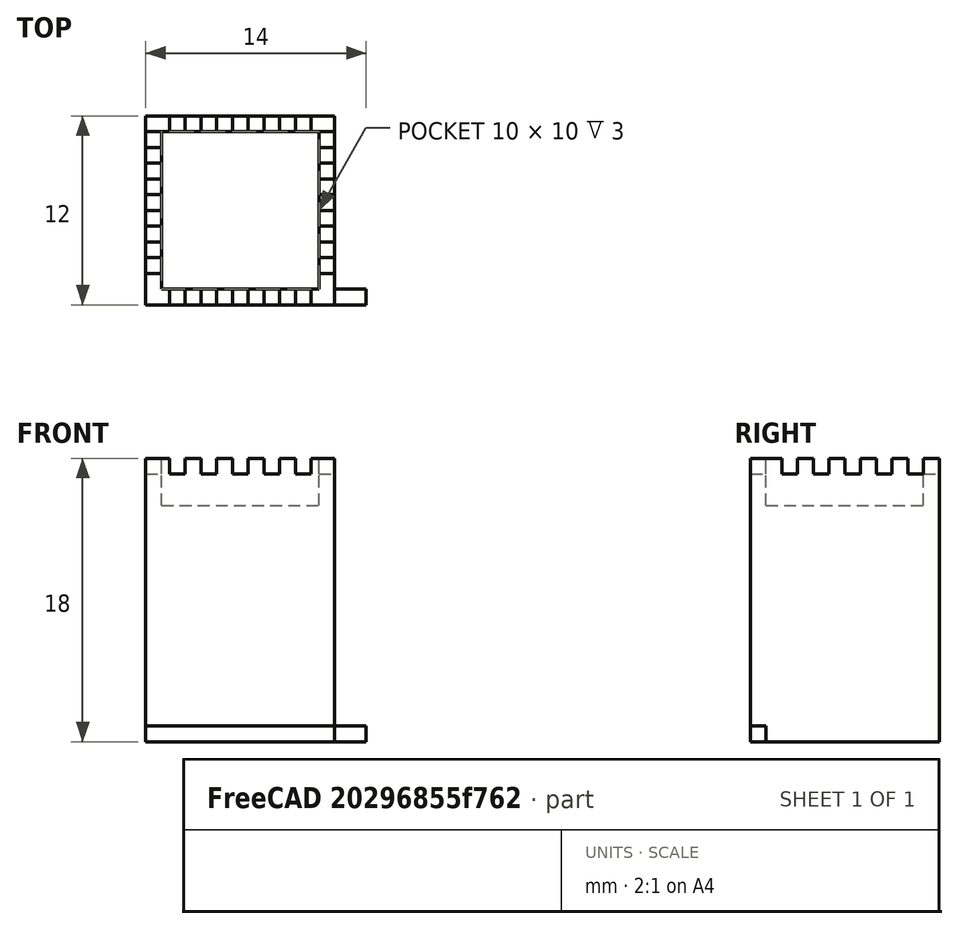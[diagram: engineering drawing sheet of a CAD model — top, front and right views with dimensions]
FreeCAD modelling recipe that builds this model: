
FCSTD DOCUMENT  (FreeCAD 1.0R39319 (Git))
Label: ojt1_t10r02_tower
License: All rights reserved
LicenseURL: https://en.wikipedia.org/wiki/All_rights_reserved
objects: Part::Box×4, Part::Cut×3, Part::FeaturePython×2
note: 7 computed .brp shape members not serialized (recipe doc carries the construction recipe); baked Part::Feature solids carry a one-line shape summary decoded from their .brp

FEATURE [Part::Box] Box  label="Cub"
  AttacherType = Attacher::AttachEngine3D
  Height = 18
  Length = 12
  Width = 12
FEATURE [Part::Box] Box001  label="Cub001"
  AttacherType = Attacher::AttachEngine3D
  Height = 8
  Length = 10
  Placement = pos=(1,1,15) rot=(0,0,1;0rad)
  Width = 10
FEATURE [Part::Cut] Cut
  Base = -> Box
  Refine = true
  Tool = -> Box001
FEATURE [Part::Box] Box002  label="Cub002"
  AttacherType = Attacher::AttachEngine3D
  Height = 1
  Length = 14
  Width = 1
FEATURE [Part::FeaturePython] Array  # Draft array (typed FeaturePython)
  AlwaysSyncPlacement = false
  Angle = 360
  ArrayType = 0
  Axis = (0,0,1)
  Base = -> Box002
  Center = (0,0,0)
  Count = 5
  ExpandArray = false
  Fuse = false
  IntervalAxis = (0,0,0)
  IntervalX = (2,0,0)
  IntervalY = (0,2,0)
  IntervalZ = (0,0,2)
  NumberCircles = 3
  NumberPolar = 5
  NumberX = 1
  NumberY = 5
  NumberZ = 1
  Placement = pos=(-1,2,17) rot=(0,0,1;0rad)
  PlacementList = 5 placements: arithmetic series from (0,0,0) step (0,2,0) to (0,8,0)
  RadialDistance = 50
  ScaleList = (5) [(1,1,1),(1,1,1),(1,1,1),(1,1,1),(1,1,1)]
  Symmetry = 1
  TangentialDistance = 25
FEATURE [Part::Box] Box003  label="Cub003"
  AttacherType = Attacher::AttachEngine3D
  Height = 1
  Length = 14
  Width = 1
FEATURE [Part::FeaturePython] Array001  # Draft array (typed FeaturePython)
  AlwaysSyncPlacement = false
  Angle = 360
  ArrayType = 0
  Axis = (0,0,1)
  Base = -> Box003
  Center = (0,0,0)
  Count = 5
  ExpandArray = false
  Fuse = false
  IntervalAxis = (0,0,0)
  IntervalX = (2,0,0)
  IntervalY = (0,2,0)
  IntervalZ = (0,0,2)
  NumberCircles = 3
  NumberPolar = 5
  NumberX = 1
  NumberY = 5
  NumberZ = 1
  Placement = pos=(10.5,-1.5,17) rot=(0,0,1;1.5708rad)
  PlacementList = 5 placements: arithmetic series from (0,0,0) step (0,2,0) to (0,8,0)
  RadialDistance = 50
  ScaleList = (5) [(1,1,1),(1,1,1),(1,1,1),(1,1,1),(1,1,1)]
  Symmetry = 1
  TangentialDistance = 25
FEATURE [Part::Cut] Cut001
  Base = -> Cut
  Refine = true
  Tool = -> Array
FEATURE [Part::Cut] Cut002
  Base = -> Cut001
  Refine = true
  Tool = -> Array001
